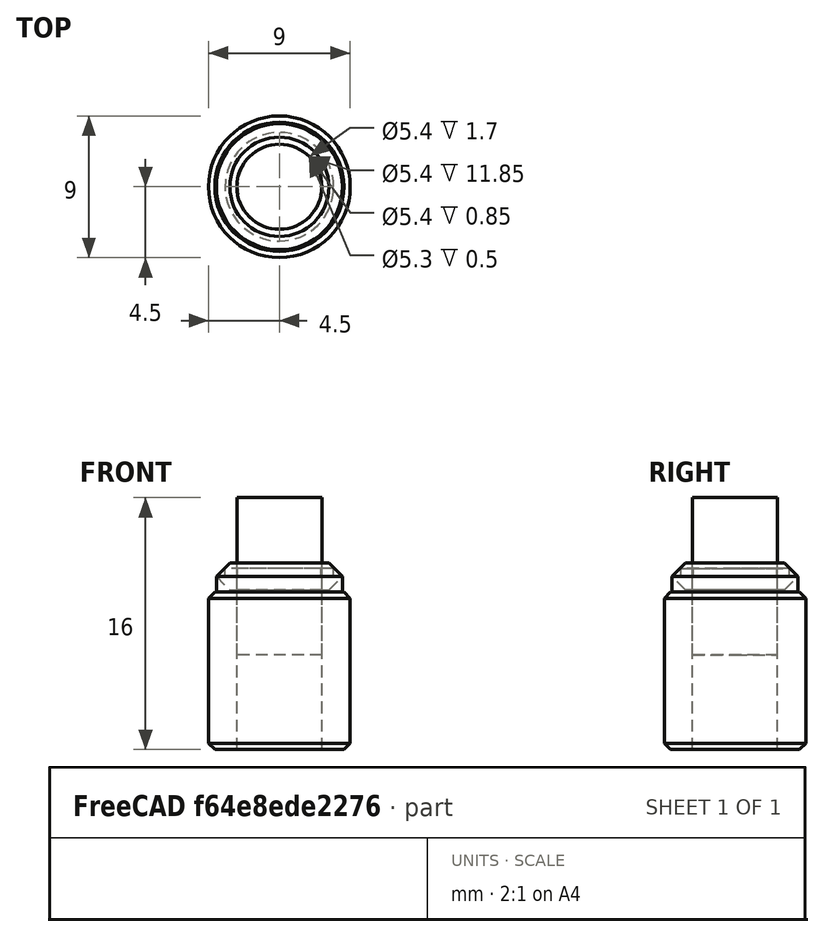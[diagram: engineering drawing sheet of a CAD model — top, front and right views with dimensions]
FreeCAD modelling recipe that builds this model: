
FCSTD DOCUMENT  (FreeCAD 0.19R24291 (Git))
Label: spacer-alt
License: Other
LicenseURL: GPL3
objects: Part::Feature×4, Part::Cylinder×4, Part::Cut×3
note: 11 computed .brp shape members not serialized (recipe doc carries the construction recipe); baked Part::Feature solids carry a one-line shape summary decoded from their .brp

FEATURE [Part::Feature] Cut008004003004014002002005003004003002003021022001002001022  label="idler-washer007"
  Placement = pos=(-11,-15,0) rot=(0,0,1;0rad)
  shape: bbox 8 x 8 x 0.85 mm, 4 faces (baked)
FEATURE [Part::Cylinder] Cylinder
  Angle = 360
  AttacherType = Attacher::AttachEngine3D
  Height = 10
  Placement = pos=(0,0,15) rot=(0,0,1;0rad)
  Radius = 2.7
FEATURE [Part::Feature] Cut008004003004014002002005003004003002003001003001022  label="spacer003"
  Placement = pos=(0,0,20) rot=(0,0,1;0rad)
  shape: bbox 8 x 8 x 1.7 mm, 5 faces (baked)
FEATURE [Part::Cylinder] Cylinder001
  Angle = 360
  AttacherType = Attacher::AttachEngine3D
  Height = 10
  Placement = pos=(0,0,15) rot=(0,0,1;0rad)
  Radius = 2.7
FEATURE [Part::Cut] Cut
  Base = -> Cut008004003004014002002005003004003002003001003001022
  Tool = -> Cylinder
FEATURE [Part::Cylinder] Cylinder002
  Angle = 360
  AttacherType = Attacher::AttachEngine3D
  Height = 10
  Placement = pos=(0,0,15) rot=(0,0,1;0rad)
  Radius = 2.7
FEATURE [Part::Cut] Cut008004003004014002002005003004003002003021022001002001023
  Base = -> Cut008004003004014002002005003004003002003021022001002001022
  Tool = -> Cylinder002
FEATURE [Part::Feature] Part__Mirroring003003003031  label="5mm-washer020"
  Placement = pos=(8.5,41,-45) rot=(0,1,0;4.71239rad)
  shape: bbox 6.9 x 6.9 x 0.5 mm, 4 faces (baked)
FEATURE [Part::Feature] Part__Mirroring005001  label="dummy-idler"
  Placement = pos=(11,35.5,0) rot=(0,0,1;0rad)
  shape: bbox 9 x 9 x 11.85 mm, 9 faces (baked)
FEATURE [Part::Cylinder] Cylinder003
  Angle = 360
  AttacherType = Attacher::AttachEngine3D
  Height = 21
  Placement = pos=(0,0,4.5) rot=(0,0,1;0rad)
  Radius = 2.7
FEATURE [Part::Cut] Cut008004003004014002002005003004003002003021022001002001024
  Base = -> Part__Mirroring005001
  Tool = -> Cylinder003
